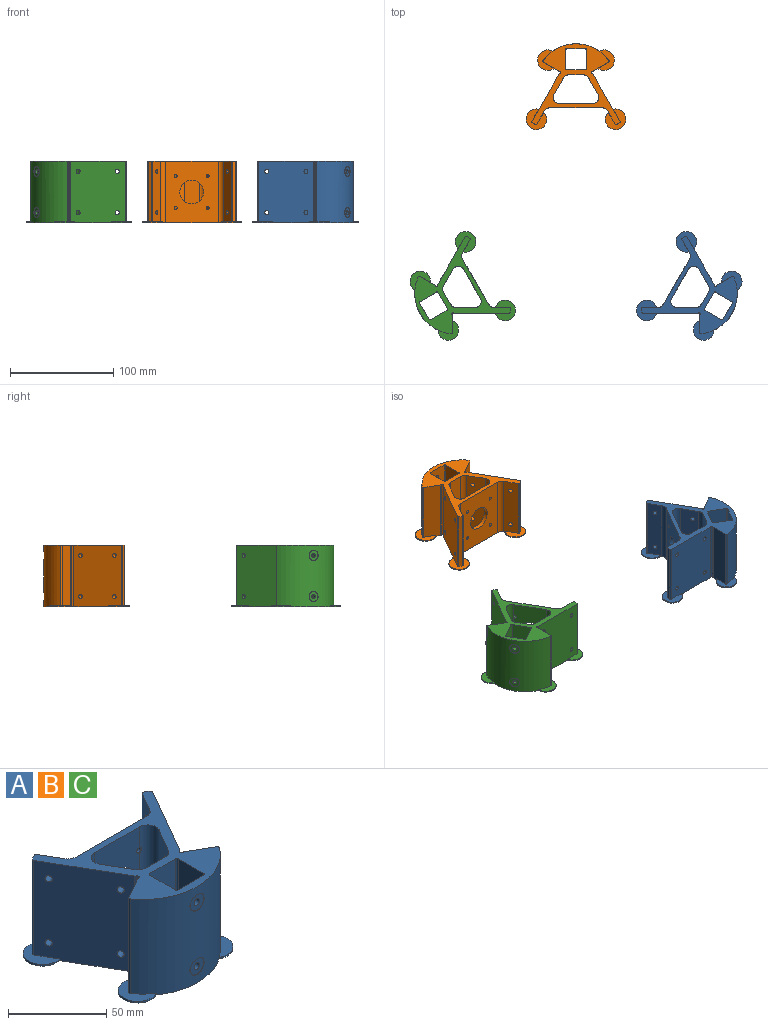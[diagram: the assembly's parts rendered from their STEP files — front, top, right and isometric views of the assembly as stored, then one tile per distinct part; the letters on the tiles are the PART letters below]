
ASSEMBLY  parts=3 mates=6
PART A: 73 faces, bbox 96.8x83.2x60 mm
  f0: plane 59x3.03mm, normal (-0.5,0.87,0), area 206.5mm2, adj f1,f2,f12,f72
  f1: cylinder r=1mm len=59mm, axis (0,0,-1), area 92.7mm2, adj f0,f9,f12,f72
  f2: cylinder r=1mm len=59mm, axis (0,0,-1), area 92.7mm2, adj f0,f12,f19,f72
  f3: cylinder r=1mm len=59mm, axis (0,0,1), area 98.7mm2, adj f8,f12,f20,f70
  f4: cylinder r=1mm len=59mm, axis (0,0,1), area 98.7mm2, adj f8,f12,f21,f68
  f5: plane 59x3.03mm, normal (0.5,0.87,0), area 206.5mm2, adj f6,f7,f12,f66
  f6: cylinder r=1mm len=59mm, axis (0,0,1), area 92.7mm2, adj f5,f10,f12,f66
  f7: cylinder r=1mm len=59mm, axis (0,0,-1), area 92.7mm2, adj f5,f12,f25,f66
  f8: cylinder r=39.5mm len=64.03mm, axis (0,0,1), area 4294.9mm2, adj f3,f4,f11,f12,f17,f63,f67,f68
  f9: plane 60x46.02mm, normal (-0.87,-0.5,0), area 3126.6mm2, adj f1,f11,f12,f42,f43,f44,f45,f60
  f10: plane 60x46.02mm, normal (0.87,-0.5,0), area 3126.6mm2, adj f6,f11,f12,f38,f39,f40,f41,f58
  f11: plane 96.84x83.16mm, normal (0,0,-1), area 2611.1mm2, adj f8,f9,f10,f18,f19,f20,f21,f22
  f12: plane 85.87x78.5mm, normal (0,0,1), area 1824.1mm2, adj f0,f1,f2,f3,f4,f5,f6,f7
  f13: cylinder r=1.75mm len=3.42mm, axis (0,1,0), area 0.4mm2, adj f18,f26
  f14: cylinder r=1.75mm len=2.93mm, axis (0,1,0), area 0.1mm2, adj f26,f27
  f15: cylinder r=1.75mm len=2.93mm, axis (0,1,0), area 0.1mm2, adj f26,f27
  f16: cylinder r=1.75mm len=3.42mm, axis (0,1,0), area 0.4mm2, adj f18,f26
  f17: cylinder r=5mm len=10mm, axis (0,1,0), area 12mm2, adj f8,f37
  f18: cylinder r=6mm len=60mm, axis (0,0,1), area 749.3mm2, adj f11,f12,f13,f16,f26,f32
  f19: plane 60x12.88mm, normal (0.87,0.5,0), area 855.1mm2, adj f2,f11,f12,f22,f42,f43,f71,f72
  f20: plane 60x14.68mm, normal (-0.5,0.87,0), area 1004.9mm2, adj f3,f11,f12,f61,f69,f70
  f21: plane 60x14.68mm, normal (0.5,0.87,0), area 1004.9mm2, adj f4,f11,f12,f59,f67,f68
  f22: cylinder r=6mm len=60mm, axis (0,0,1), area 377mm2, adj f11,f12,f19,f23
  f23: plane 60x50.81mm, normal (0,1,0), area 2605.6mm2, adj f11,f12,f22,f24,f47,f48,f49,f50
  f24: cylinder r=6mm len=60mm, axis (0,0,1), area 377mm2, adj f11,f12,f23,f25
  f25: plane 60x12.88mm, normal (-0.87,0.5,0), area 855.1mm2, adj f7,f11,f12,f24,f38,f39,f65,f66
  f26: plane 60x34.5mm, normal (0,-1,0), area 1507.4mm2, adj f11,f12,f13,f14,f15,f16,f18,f27
  f27: cylinder r=6mm len=60mm, axis (0,0,1), area 751.6mm2, adj f11,f12,f14,f15,f26,f28
  f28: plane 60x16mm, normal (0.87,0.5,0), area 1084.6mm2, adj f11,f12,f27,f29,f44,f45
  f29: cylinder r=6mm len=60mm, axis (0,0,1), area 377mm2, adj f11,f12,f28,f30
  f30: plane 60x13.86mm, normal (0,1,0), area 831.5mm2, adj f11,f12,f29,f31
  f31: cylinder r=6mm len=60mm, axis (0,0,1), area 377mm2, adj f11,f12,f30,f32
  f32: plane 60x16mm, normal (-0.87,0.5,0), area 1084.6mm2, adj f11,f12,f18,f31,f40,f41
  f33: plane 60x18.4mm, normal (0,-1,0), area 1104mm2, adj f11,f12,f54,f55
  f34: plane 60x18.4mm, normal (1,0,0), area 1104mm2, adj f11,f12,f52,f54
  f35: plane 60x18.4mm, normal (0,1,0), area 1080.1mm2, adj f11,f12,f46,f52,f53,f62
  f36: plane 60x18.4mm, normal (-1,0,0), area 1104mm2, adj f11,f12,f53,f55
  f37: plane 10x10mm, normal (0,-1,0), area 66.6mm2, adj f17,f46
  f38: cylinder r=1.95mm len=6.71mm, axis (0.87,-0.5,0), area 67.4mm2, adj f10,f25
  f39: cylinder r=1.95mm len=6.71mm, axis (0.87,-0.5,0), area 67.4mm2, adj f10,f25
  f40: cylinder r=1.95mm len=6.71mm, axis (0.87,-0.5,0), area 67.4mm2, adj f10,f32
  f41: cylinder r=1.95mm len=6.71mm, axis (0.87,-0.5,0), area 67.4mm2, adj f10,f32
  f42: cylinder r=1.95mm len=6.71mm, axis (-0.87,-0.5,0), area 67.4mm2, adj f9,f19
  f43: cylinder r=1.95mm len=6.71mm, axis (-0.87,-0.5,0), area 67.4mm2, adj f9,f19
  f44: cylinder r=1.95mm len=6.71mm, axis (-0.87,-0.5,0), area 67.4mm2, adj f9,f28
  f45: cylinder r=1.95mm len=6.71mm, axis (-0.87,-0.5,0), area 67.4mm2, adj f9,f28
  f46: cylinder r=1.95mm len=4.3mm, axis (0,-1,0), area 52.7mm2, adj f35,f37
  f47: cylinder r=1.47mm len=4mm, axis (0,1,0), area 37.1mm2, adj f23,f26
  f48: cylinder r=1.47mm len=4mm, axis (0,1,0), area 37.1mm2, adj f23,f26
  f49: cylinder r=1.47mm len=4mm, axis (0,1,0), area 37.1mm2, adj f23,f26
  f50: cylinder r=1.47mm len=4mm, axis (0,1,0), area 37.1mm2, adj f23,f26
  f51: cylinder r=11.5mm len=23mm, axis (0,1,0), area 289mm2, adj f23,f26
  f52: cylinder r=1mm len=60mm, axis (0,0,1), area 94.2mm2, adj f11,f12,f34,f35
  f53: cylinder r=1mm len=60mm, axis (0,0,1), area 94.2mm2, adj f11,f12,f35,f36
  f54: cylinder r=1mm len=60mm, axis (0,0,1), area 94.2mm2, adj f11,f12,f33,f34
  f55: cylinder r=1mm len=60mm, axis (0,0,1), area 94.2mm2, adj f11,f12,f33,f36
  f56: cylinder r=1mm len=60mm, axis (0,0,1), area 164.5mm2, adj f11,f12,f58,f59
  f57: cylinder r=1mm len=60mm, axis (0,0,1), area 164.5mm2, adj f11,f12,f60,f61
  f58: cylinder r=2mm len=60mm, axis (0,0,1), area 70.3mm2, adj f10,f11,f12,f56
  f59: cylinder r=2mm len=60mm, axis (0,0,1), area 70.3mm2, adj f11,f12,f21,f56
  f60: cylinder r=2mm len=60mm, axis (0,0,1), area 70.3mm2, adj f9,f11,f12,f57
  f61: cylinder r=2mm len=60mm, axis (0,0,1), area 70.3mm2, adj f11,f12,f20,f57
  f62: cylinder r=1.95mm len=4.3mm, axis (0,-1,0), area 52.7mm2, adj f35,f64
  f63: cylinder r=5mm len=10mm, axis (0,1,0), area 12mm2, adj f8,f64
  f64: plane 10x10mm, normal (0,-1,0), area 66.6mm2, adj f62,f63
  f65: cylinder r=10mm len=20mm, axis (0,0,-1), area 57.3mm2, adj f10,f11,f25,f66
  f66: plane 20x20mm, normal (0,0,1), area 232.8mm2, adj f5,f6,f7,f10,f25,f65
  f67: cylinder r=10mm len=20mm, axis (0,0,-1), area 42.7mm2, adj f8,f11,f21,f68
  f68: plane 20x15.97mm, normal (0,0,1), area 160.7mm2, adj f4,f8,f21,f67
  f69: cylinder r=10mm len=20mm, axis (0,0,-1), area 42.7mm2, adj f8,f11,f20,f70
  f70: plane 20x15.97mm, normal (0,0,1), area 160.7mm2, adj f3,f8,f20,f69
  f71: cylinder r=10mm len=20mm, axis (0,0,-1), area 57.3mm2, adj f9,f11,f19,f72
  f72: plane 20x20mm, normal (0,0,1), area 232.8mm2, adj f0,f1,f2,f9,f19,f71
PART B: same geometry as A
PART C: same geometry as A
PLACE A rot(axis=(0,0,1),60deg) t=(113.14,-115.17,60)mm
PLACE B rot(axis=(0,0,1),180deg) t=(0,80.79,60)mm
PLACE C rot(axis=(0,0,-1),60deg) t=(-113.14,-115.17,60)mm
MATE planar A.f10 <-> B.f9  axis (0.87,0.5,0) through (120.83,-85.58,30.13)mm
MATE planar B.f12 <-> C.f12  axis (0,0,1) through (0,90,60)mm
MATE planar A.f12 <-> B.f12  axis (0,0,1) through (121.11,-119.77,60)mm
MATE parallel B.f21 <-> C.f20  axis (-0.5,-0.87,0) through (-24.34,102.77,30.36)mm
MATE planar C.f10 <-> A.f9  axis (0,-1,0) through (-91.36,-136.63,30.13)mm
MATE planar B.f10 <-> C.f9  axis (-0.87,0.5,0) through (-29.48,72.66,30.13)mm
